# Revit family: Sliding_Gate_Automation_Residential_Ditec_Neos_plus_1000
name_source: partatom
category: Electrical Fixtures
revit_build: Autodesk Revit Architecture 2014 (Build: 20130308_1515(x64)
units: mm (PartAtom-declared; Revit-internal decimal feet)

## types (1)
- Sliding_Gate_Automation_Residential_Ditec_Neos_plus_1000
    Closing speed = 0.1 - 0.19 m/s
    Control panel = CS12M (built-in)
    Description = NeoS+ 1000  (also available: 300/400/600)
    Design country = Italy
    Duty class = 4 - intensive
    Edition number = 1
    Electromechanical actuator = for sliding gates up to
1000 kg
    Gate Height = 1200 mm  [stored 3.93701 ft]
    Gate Length = 2500 mm  [stored 8.2021 ft]
    Gate Visibility = Yes
    Installation instructions = http://ftp.ditec.it
    Intermittent operation = S2 = 30 min, S3 = 50%
    Manufacturer country = China
    Manufacturer name = Ditec
    Material main = Steel
    Material secondary = Plastic
    Maximum capacity = 1000 kg
    Maximum opening = 20m
    Nominal height = 325
    Nominal width = 335
    Opening speed = 0.1 - 0.19 m/s
    Operating temperature = -20°C / +55°C (-35°C / +55°C with NIO enabled)
    Power input = 2A
    Power supply = 230 V AC, 50/60 Hz
    Product Guid = 4d1a2df7-523c-4302-893f-15eee6c94ea3
    Product SKU = dit-neos
    Product data url = http://bimobject.com
    Product dimensions (mm) = 335x220x325
    Product family = Gate Automation & Barriers
    Product group = Sliding Gates
    Protection rating = IP 24D
    QR code = http://bimobject.com
    Release for manual opening = key-operated
    Stroke control = limit switch + virtual encoder
    Torque/Thrust = 1000 N
    Weight Net (Kg) = 0

note: [stored X ft] marks values corroborated as IEEE doubles in the binary element streams (Revit-internal decimal feet)

## geometry (parser evidence)
native form markers: Blend x2, Sweep x11
no freeform markers — native parametric forms only
